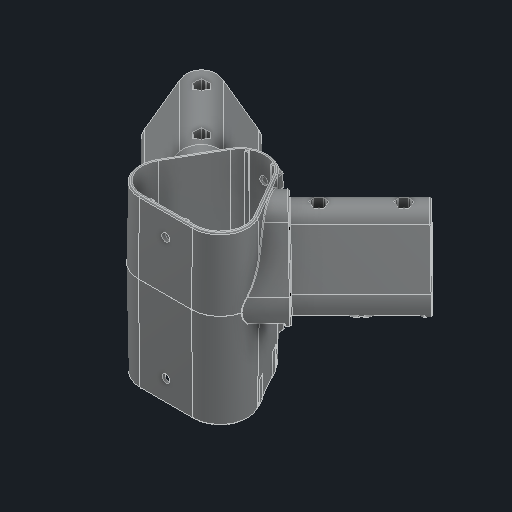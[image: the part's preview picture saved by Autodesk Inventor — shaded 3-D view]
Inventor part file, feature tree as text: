
AUTODESK INVENTOR PART (.ipt)
format: ipt  version: 2025 (Build 290162000, 162)  size: 2,503,168 bytes
history: native  units: in
note: dims shown in document units (in); Inventor stores cm internally (conversion verified against a paired STEP export)
features: fillet x1
ambient origin geometry x8: Origin, YZ Plane, XZ Plane, XY Plane, X Axis, Y Axis, Z Axis, Center Point
bodies: Solid1 (feature_tree)
feature tree (1):
  fillet  "Fillet139"  [1 undecoded]
note: 1 required parameter value undecoded (feature->parameter linkage not recoverable at this tier; creation-order binding heuristic only, values carry confidence <= 0.55)
